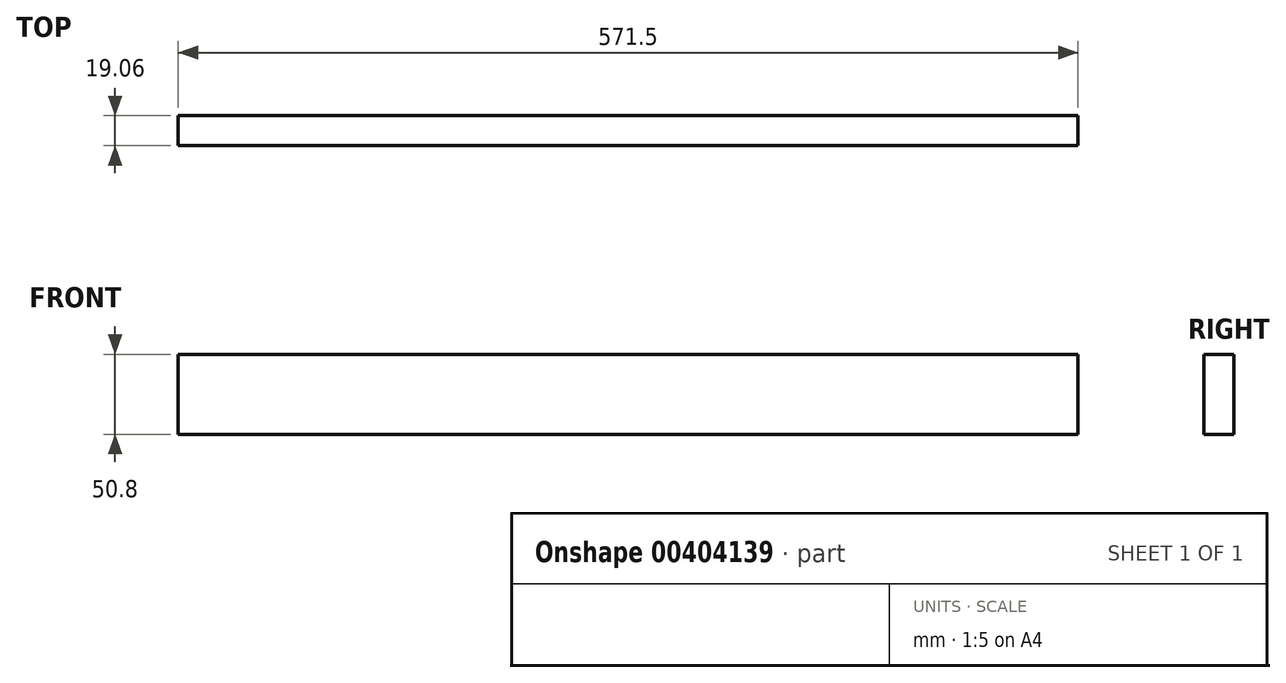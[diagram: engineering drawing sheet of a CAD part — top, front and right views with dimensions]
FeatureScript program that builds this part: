
annotation { "Feature Type Name" : "Feature", "Feature Type Description" : "" }
export const myFeature = defineFeature(function(context is Context, id is Id, definition is map)
    precondition{}
    {
        {
            var Q0;
            Q0=qCreatedBy(makeId("Front.planeOp"),FACE);
            var sketch = newSketch(context, id + "F0", { "sketchPlane" : qUnion([Q0])});
            skLineSegment(sketch, "E0.bottom", {"start": v(12.19, 0) * mm, "end": v(583.69, 0) * mm});
            skLineSegment(sketch, "E0.top", {"start": v(12.19, 50.8) * mm, "end": v(583.69, 50.8) * mm});
            skLineSegment(sketch, "E0.left", {"start": v(12.19, 0) * mm, "end": v(12.19, 50.8) * mm});
            skLineSegment(sketch, "E0.right", {"start": v(583.69, 0) * mm, "end": v(583.69, 50.8) * mm});
            skSolve(sketch);
        }
        {
            var Q0;
            Q0 = qSketchRegion(id + "F0", true);
            extrude(context, id + "F1", {"entities" : qUnion([Q0]), "endBound" : BoundingType.SYMMETRIC, "depth" : 19.05 * mm});
        }
    });
